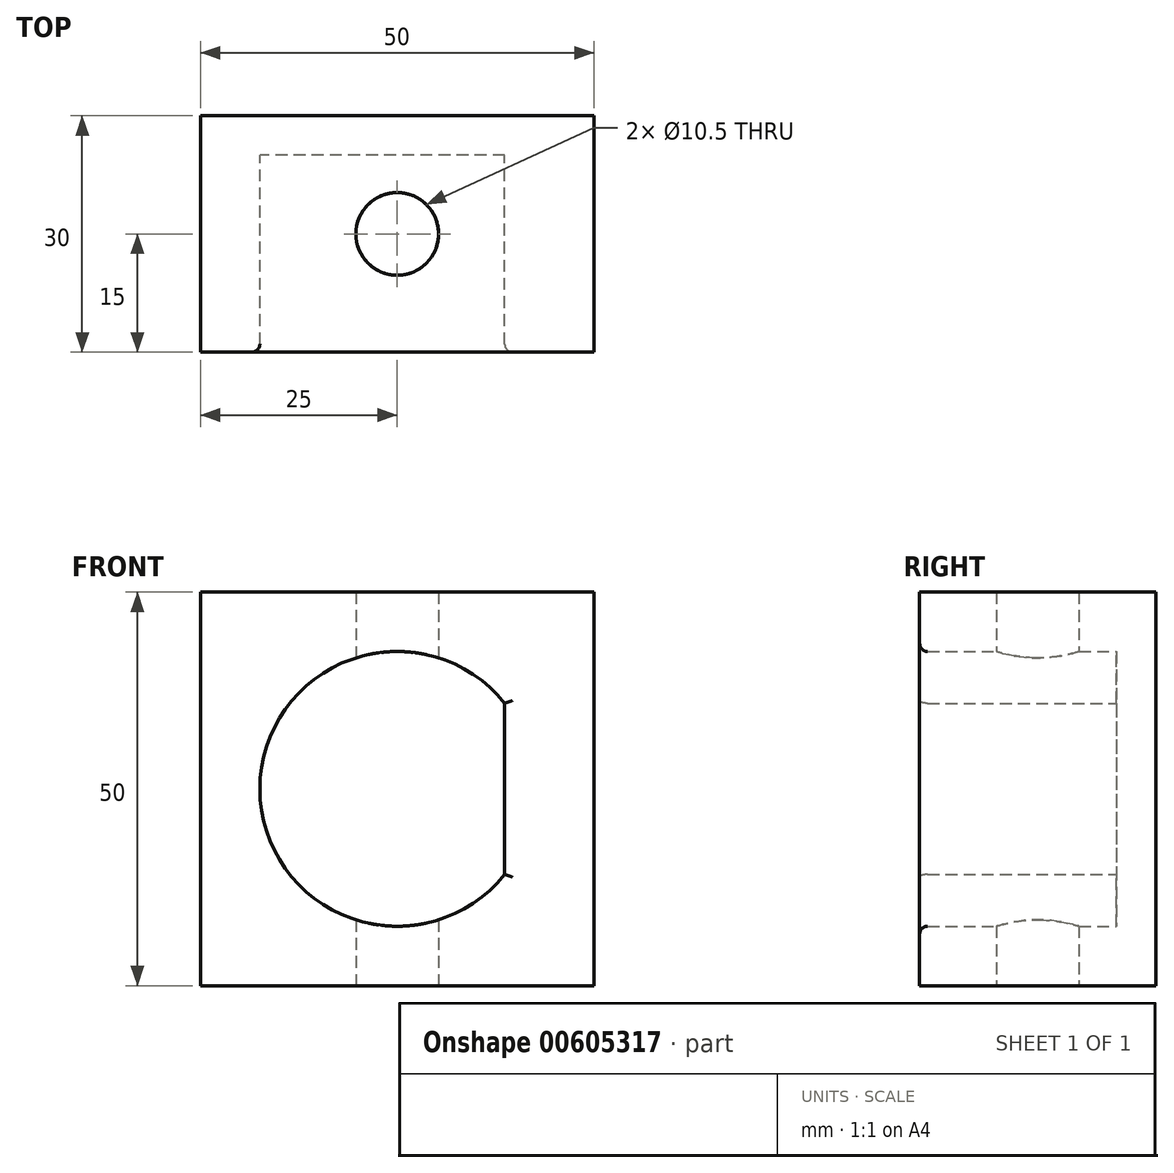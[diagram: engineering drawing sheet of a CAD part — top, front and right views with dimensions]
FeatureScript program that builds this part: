
annotation { "Feature Type Name" : "Feature", "Feature Type Description" : "" }
export const myFeature = defineFeature(function(context is Context, id is Id, definition is map)
    precondition{}
    {
        {
            var Q0;
            Q0=qCreatedBy(makeId("Front.planeOp"),FACE);
            var sketch = newSketch(context, id + "F0", { "sketchPlane" : qUnion([Q0])});
            skLineSegment(sketch, "E0.bottom", {"start": v(-25, -25) * mm, "end": v(25, -25) * mm});
            skLineSegment(sketch, "E0.top", {"start": v(-25, 25) * mm, "end": v(25, 25) * mm});
            skLineSegment(sketch, "E0.left", {"start": v(-25, -25) * mm, "end": v(-25, 25) * mm});
            skLineSegment(sketch, "E0.right", {"start": v(25, -25) * mm, "end": v(25, 25) * mm});
            skPoint(sketch, "E0.middle", {"position": v(0, 0) * mm});
            skArc(sketch, "E1", {"start": v(13.65, 10.87) * mm, "mid": v(-17.45, 0) * mm, "end": v(13.65, -10.87) * mm});
            skLineSegment(sketch, "E2", {"start": v(13.65, 10.87) * mm, "end": v(13.65, -10.87) * mm});
            skSolve(sketch);
        }
        {
            var Q0;
            Q0 = qSketchRegion(id + "F0", true);
            extrude(context, id + "F1", {"entities" : qUnion([Q0]), "depth" : 30 * mm, "offsetDistance" : 25 * mm});
        }
        {
            var Q0;
            Q0=makeQuery(id+"F1.opExtrude","SWEPT_FACE",FACE,{"disambiguationData":[OSD([sQuery(id+"F0.wireOp",EDGE,"E0.bottom")])]});
            var sketch = newSketch(context, id + "F2", { "sketchPlane" : qUnion([Q0])});
            skCircle(sketch, "E3", {"center": v(0, 15) * mm, "radius": 8 * mm});
            skSolve(sketch);
        }
        {
            var Q0;
            Q0=makeQuery(id+"F1.opExtrude","CAP_EDGE",EDGE,{"disambiguationData":[OSD([sQuery(id+"F0.wireOp",EDGE,"E2")])],"isStart":false});
            var Q1;
            Q1=makeQuery(id+"F1.opExtrude","CAP_EDGE",EDGE,{"disambiguationData":[OSD([sQuery(id+"F0.wireOp",EDGE,"E1")])],"isStart":false});
            fillet(context, id + "F3", {"entities" : qUnion([Q0, Q1]), "radius" : 1 * mm, "tangentPropagation" : true, "allowEdgeOverflow" : false});
        }
        {
            var Q0;
            Q0=makeQuery(id+"F0.imprint","IMPRINT",FACE,{"disambiguationData":[TD([[makeQuery(id+"F0.imprint","IMPRINT",EDGE,{"derivedFrom":sQuery(id+"F0.wireOp",EDGE,"E0.bottom")}),1.0]])]});
            var sketch = newSketch(context, id + "F4", { "sketchPlane" : qUnion([Q0])});
            skLineSegment(sketch, "E4.bottom", {"start": v(25, -25) * mm, "end": v(-25, -25) * mm});
            skLineSegment(sketch, "E4.top", {"start": v(25, 25) * mm, "end": v(-25, 25) * mm});
            skLineSegment(sketch, "E4.left", {"start": v(25, -25) * mm, "end": v(25, 25) * mm});
            skLineSegment(sketch, "E4.right", {"start": v(-25, -25) * mm, "end": v(-25, 25) * mm});
            skPoint(sketch, "E4.middle", {"position": v(0, 0) * mm});
            skSolve(sketch);
        }
        {
            var Q0;
            Q0 = qSketchRegion(id + "F4", true);
            extrude(context, id + "F5", {"entities" : qUnion([Q0]), "operationType" : NewBodyOperationType.ADD, "depth" : 5 * mm, "offsetDistance" : 25 * mm});
        }
        {
            var Q0;
            Q0=sQuery(id+"F2.wireOp",VERTEX,"E3.center");
            var Q1;
            Q1=makeQuery(id+"F1.opExtrude","SWEPT_BODY",BODY,{"disambiguationData":[OSD([sQuery(id+"F0.wireOp",EDGE,"E0.bottom"),sQuery(id+"F0.wireOp",EDGE,"E0.top"),sQuery(id+"F0.wireOp",EDGE,"E0.left"),sQuery(id+"F0.wireOp",EDGE,"E0.right"),sQuery(id+"F0.wireOp",EDGE,"E1"),sQuery(id+"F0.wireOp",EDGE,"E2")])]});
            hole(context, id + "F6", {"style" : HoleStyle.SIMPLE, "endStyle" : HoleEndStyle.THROUGH, "standardTappedOrClearance" : lookupTablePath({ "standard" : "ISO", "engagement" : "75%", "pitch" : "1.5 mm", "size" : "M12", "type" : "Tapped" }), "standardBlindInLast" : lookupTablePath({ "standard" : "ISO", "engagement" : "75%", "pitch" : "1.5 mm", "size" : "M12", "type" : "Tapped" }), "holeDiameter" : 10.5 * mm, "majorDiameter" : 12 * mm, "showTappedDepth" : true, "isTappedThrough" : true, "tappedDepth" : 12 * mm, "tapClearance" : 3, "locations" : qUnion([Q0]), "scope" : qUnion([Q1])});
        }
    });
